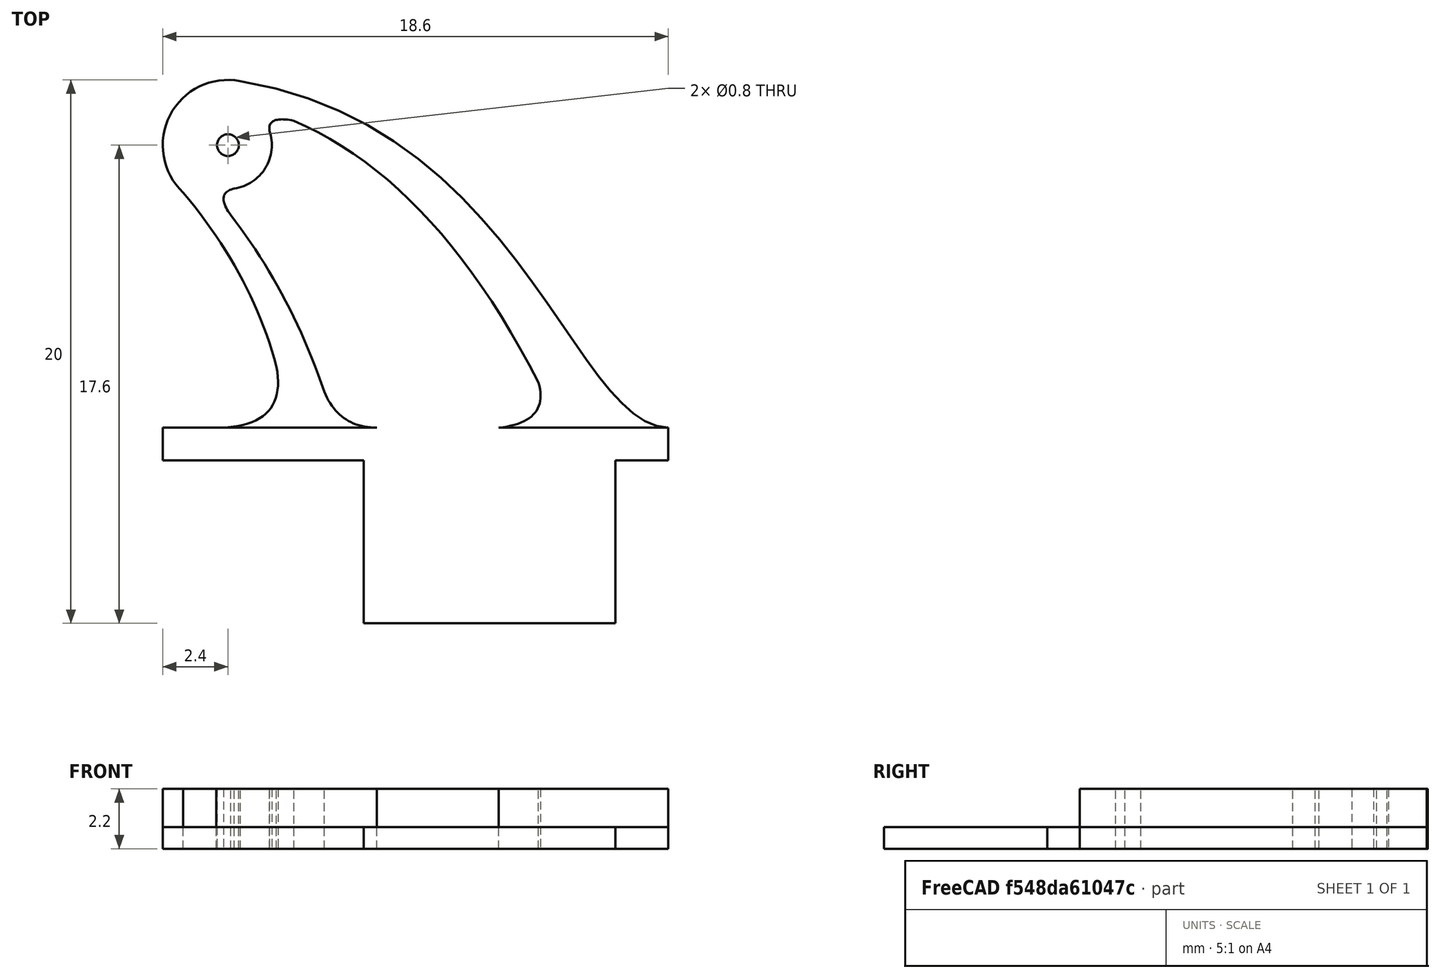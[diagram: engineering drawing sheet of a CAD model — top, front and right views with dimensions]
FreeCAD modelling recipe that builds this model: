
FCSTD DOCUMENT  (FreeCAD 0.20R0.20.2)
Label: 008
License: All rights reserved
LicenseURL: http://en.wikipedia.org/wiki/All_rights_reserved
objects: Sketcher::SketchObject×2, Part::Extrusion×2
note: 4 computed .brp shape members not serialized (recipe doc carries the construction recipe); baked Part::Feature solids carry a one-line shape summary decoded from their .brp

FEATURE [Sketcher::SketchObject] Sketch  label="main"
  FullyConstrained = true
  sketch-geometry (25):
    g0: LineSegment StartX=12.0586 StartY=-6 StartZ=0 EndX=12.0586 EndY=0 EndZ=0
    g1: LineSegment StartX=2.8 StartY=-6 StartZ=0 EndX=2.8 EndY=0 EndZ=0
    g2: LineSegment StartX=2.8 StartY=-6 StartZ=0 EndX=12.0586 EndY=-6 EndZ=0
    g3: LineSegment StartX=12.0586 StartY=0 StartZ=0 EndX=14 EndY=0 EndZ=0
    g4: LineSegment StartX=2.8 StartY=0 StartZ=0 EndX=0 EndY=0 EndZ=0
    g5: LineSegment StartX=14 StartY=0 StartZ=0 EndX=14 EndY=1.2 EndZ=0
    g6: LineSegment StartX=0 StartY=0 StartZ=0 EndX=-4.6 EndY=0 EndZ=0
    g7: Circle CenterX=-2.2 CenterY=11.6 CenterZ=0 NormalX=0 NormalY=0 NormalZ=1 AngleXU=0 Radius=0.4
    g8-g11: Circle x4 (B-spline internal-alignment scaffolding for g12; pole/knot coordinates omitted)
    g12: BSplineCurve PolesCount=4 KnotsCount=2 Degree=3 IsPeriodic=0
    g13: GeomPoint X=-1.74436 Y=13.9564 Z=0
    g14: GeomPoint X=14 Y=1.2 Z=0
    g15: ArcOfCircle CenterX=-2.2 CenterY=11.6 CenterZ=0 NormalX=0 NormalY=0 NormalZ=1 AngleXU=0 Radius=2.4 StartAngle=1.37979 EndAngle=3.95565
    g16: LineSegment StartX=-2.62672 StartY=1.2 StartZ=0 EndX=-4.6 EndY=1.2 EndZ=0
    g17: LineSegment StartX=-4.6 StartY=0 StartZ=0 EndX=-4.6 EndY=1.2 EndZ=0
    g18: Circle CenterX=-2.62672 CenterY=1.2 CenterZ=0 NormalX=0 NormalY=0 NormalZ=1 AngleXU=0 Radius=1
    g19: Circle CenterX=0 CenterY=1.2 CenterZ=0 NormalX=0 NormalY=0 NormalZ=1 AngleXU=0 Radius=1
    g20: Circle CenterX=-0.413885 CenterY=3.44541 CenterZ=0 NormalX=0 NormalY=0 NormalZ=1 AngleXU=0 Radius=1
    g21: BSplineCurve PolesCount=3 KnotsCount=2 Degree=2 IsPeriodic=0
    g22: GeomPoint X=-2.62672 Y=1.2 Z=0
    g23: GeomPoint X=-0.413885 Y=3.44541 Z=0
    g24: BSplineCurve PolesCount=3 KnotsCount=2 Degree=2 IsPeriodic=0
  constraints (52):
    c: Vertical(g0)
    c: Vertical(g1)
    c: Block(g1)
    c: Block(g0)
    c: Distance(g1) = 6
    c: Coincident(g2,g1)
    c: Horizontal(g2)
    c: Coincident(g0,g2)
    c: Block(g2)
    c: Coincident(g3,g0)
    c: Horizontal(g3)
    c: Coincident(g4,g1)
    c: Horizontal(g4)
    c: Block(g3)
    c: Block(g4)
    c: Coincident(g5,g3)
    c: Vertical(g5)
    c: Distance(g5) = 1.2
    c: Coincident(g6,g4)
    c: Horizontal(g6)
    c: Distance(g6) = 4.6
    c: Block(g7)
    c: Weight(g8) = 1
    c: Equal(g8,g9)
    c: Equal(g8,g10)
    c: Equal(g8,g11)
    c: Coincident(g12,g5)
    c: InternalAlignment(g8-g11 -> g12) x4
    c: InternalAlignment(g13,g12)
    c: InternalAlignment(g14,g12)
    c: Block(g12)
    c: Coincident(g15,g7)
    c: Coincident(g15,g12)
    c: Coincident(g15,g24)
    c: Block(g15)
    c: Horizontal(g16)
    c: Coincident(g17,g6)
    c: Vertical(g17)
    c: Coincident(g17,g16)
    c: Weight(g18) = 1
    c: Equal(g18,g19)
    c: Equal(g18,g20)
    c: InternalAlignment(g18,g21)
    c: InternalAlignment(g19,g21)
    c: InternalAlignment(g20,g21)
    c: InternalAlignment(g22,g21)
    c: InternalAlignment(g23,g21)
    c: Block(g16)
    c: Coincident(g16,g21)
    c: Coincident(g21,g24)
    c: Block(g24)
    c: Block(g21)
FEATURE [Part::Extrusion] Extrude
  Base = -> Sketch
  Dir = (0,0,1)
  DirMode = 2
  FaceMakerClass = Part::FaceMakerBullseye
  LengthFwd = 0.8
  LengthRev = 0
  Solid = true
  Symmetric = false
FEATURE [Sketcher::SketchObject] Sketch001  label="main001"
  FullyConstrained = false
  sketch-geometry (45):
    g0: Circle CenterX=-2.2 CenterY=11.6 CenterZ=0 NormalX=0 NormalY=0 NormalZ=1 AngleXU=0 Radius=0.4
    g1-g4: Circle x4 (B-spline internal-alignment scaffolding for g5; pole/knot coordinates omitted)
    g5: BSplineCurve PolesCount=4 KnotsCount=2 Degree=3 IsPeriodic=0
    g6: GeomPoint X=-1.74436 Y=13.9564 Z=0
    g7: GeomPoint X=14 Y=1.2 Z=0
    g8: ArcOfCircle CenterX=-2.2 CenterY=11.6 CenterZ=0 NormalX=0 NormalY=0 NormalZ=1 AngleXU=0 Radius=2.4 StartAngle=1.37979 EndAngle=3.95565
    g9: Circle CenterX=-2.62672 CenterY=1.2 CenterZ=0 NormalX=0 NormalY=0 NormalZ=1 AngleXU=0 Radius=1
    g10: Circle CenterX=0 CenterY=1.2 CenterZ=0 NormalX=0 NormalY=0 NormalZ=1 AngleXU=0 Radius=1
    g11: Circle CenterX=-0.413885 CenterY=3.44541 CenterZ=0 NormalX=0 NormalY=0 NormalZ=1 AngleXU=0 Radius=1
    g12: BSplineCurve PolesCount=3 KnotsCount=2 Degree=2 IsPeriodic=0
    g13: GeomPoint X=-2.62672 Y=1.2 Z=0
    g14: GeomPoint X=-0.413885 Y=3.44541 Z=0
    g15: BSplineCurve PolesCount=3 KnotsCount=2 Degree=2 IsPeriodic=0
    g16: Circle CenterX=1.34801 CenterY=2.51783 CenterZ=0 NormalX=0 NormalY=0 NormalZ=1 AngleXU=0 Radius=1
    g17: Circle CenterX=1.8831 CenterY=1.2 CenterZ=0 NormalX=0 NormalY=0 NormalZ=1 AngleXU=0 Radius=1
    g18: Circle CenterX=3.28198 CenterY=1.2 CenterZ=0 NormalX=0 NormalY=0 NormalZ=1 AngleXU=0 Radius=1
    g19: BSplineCurve PolesCount=3 KnotsCount=2 Degree=2 IsPeriodic=0
    g20: GeomPoint X=1.34801 Y=2.51783 Z=0
    g21: GeomPoint X=3.28198 Y=1.2 Z=0
    g22: Circle CenterX=9.22372 CenterY=2.86164 CenterZ=0 NormalX=0 NormalY=0 NormalZ=1 AngleXU=0 Radius=1
    g23: Circle CenterX=9.64409 CenterY=1.39848 CenterZ=0 NormalX=0 NormalY=0 NormalZ=1 AngleXU=0 Radius=1
    g24: Circle CenterX=7.76214 CenterY=1.2 CenterZ=0 NormalX=0 NormalY=0 NormalZ=1 AngleXU=0 Radius=1
    g25: BSplineCurve PolesCount=3 KnotsCount=2 Degree=2 IsPeriodic=0
    g26: GeomPoint X=9.22372 Y=2.86164 Z=0
    g27: GeomPoint X=7.76214 Y=1.2 Z=0
    g28: LineSegment StartX=-2.62672 StartY=1.2 StartZ=0 EndX=3.28198 EndY=1.2 EndZ=0
    g29: LineSegment StartX=7.76214 StartY=1.2 StartZ=0 EndX=14 EndY=1.2 EndZ=0
    g30: Circle CenterX=-0.671756 CenterY=12.1251 CenterZ=0 NormalX=0 NormalY=0 NormalZ=1 AngleXU=0 Radius=1
    g31: Circle CenterX=-0.754831 CenterY=12.699 CenterZ=0 NormalX=0 NormalY=0 NormalZ=1 AngleXU=0 Radius=1
    g32: Circle CenterX=0.224587 CenterY=12.4971 CenterZ=0 NormalX=0 NormalY=0 NormalZ=1 AngleXU=0 Radius=1
    g33: BSplineCurve PolesCount=3 KnotsCount=2 Degree=2 IsPeriodic=0
    g34: GeomPoint X=-0.671756 Y=12.1251 Z=0
    g35: GeomPoint X=0.224587 Y=12.4971 Z=0
    g36: Circle CenterX=-2.10085 CenterY=9.02995 CenterZ=0 NormalX=0 NormalY=0 NormalZ=1 AngleXU=0 Radius=1
    g37: Circle CenterX=-2.68572 CenterY=9.84108 CenterZ=0 NormalX=0 NormalY=0 NormalZ=1 AngleXU=0 Radius=1
    g38: Circle CenterX=-1.96262 CenterY=10.0016 CenterZ=0 NormalX=0 NormalY=0 NormalZ=1 AngleXU=0 Radius=1
    g39: BSplineCurve PolesCount=3 KnotsCount=2 Degree=2 IsPeriodic=0
    g40: GeomPoint X=-2.10085 Y=9.02995 Z=0
    g41: GeomPoint X=-1.96262 Y=10.0016 Z=0
    g42: ArcOfCircle CenterX=-2.2 CenterY=11.6 CenterZ=0 NormalX=0 NormalY=0 NormalZ=1 AngleXU=0 Radius=1.61593 StartAngle=4.85982 EndAngle=6.61413
    g43: BSplineCurve PolesCount=3 KnotsCount=2 Degree=2 IsPeriodic=0
    g44: BSplineCurve PolesCount=3 KnotsCount=2 Degree=2 IsPeriodic=0
  constraints (76):
    c: Block(g0)
    c: Weight(g1) = 1
    c: Equal(g1,g2)
    c: Equal(g1,g3)
    c: Equal(g1,g4)
    c: InternalAlignment(g1-g4 -> g5) x4
    c: InternalAlignment(g6,g5)
    c: InternalAlignment(g7,g5)
    c: Block(g5)
    c: Coincident(g8,g0)
    c: Coincident(g8,g5)
    c: Coincident(g8,g15)
    c: Block(g8)
    c: Weight(g9) = 1
    c: Equal(g9,g11)
    c: InternalAlignment(g9,g12)
    c: InternalAlignment(g10,g12)
    c: InternalAlignment(g11,g12)
    c: InternalAlignment(g13,g12)
    c: InternalAlignment(g14,g12)
    c: Coincident(g12,g15)
    c: Block(g15)
    c: Block(g12)
    c: Weight(g16) = 1
    c: Equal(g16,g17)
    c: Equal(g16,g18)
    c: InternalAlignment(g16,g19)
    c: InternalAlignment(g17,g19)
    c: InternalAlignment(g18,g19)
    c: InternalAlignment(g20,g19)
    c: InternalAlignment(g21,g19)
    c: Block(g19)
    c: Weight(g22) = 1
    c: Coincident(g25,g43)
    c: Equal(g22,g23)
    c: Equal(g22,g24)
    c: InternalAlignment(g22,g25)
    c: InternalAlignment(g23,g25)
    c: InternalAlignment(g24,g25)
    c: InternalAlignment(g26,g25)
    c: InternalAlignment(g27,g25)
    c: Block(g25)
    c: Coincident(g28,g19)
    c: Horizontal(g28)
    c: Coincident(g29,g25)
    c: Horizontal(g29)
    c: Weight(g30) = 1
    c: Equal(g30,g31)
    c: Equal(g30,g32)
    c: InternalAlignment(g30,g33)
    c: InternalAlignment(g31,g33)
    c: InternalAlignment(g32,g33)
    c: InternalAlignment(g34,g33)
    c: InternalAlignment(g35,g33)
    c: Weight(g36) = 1
    c: Equal(g36,g37)
    c: Equal(g36,g38)
    c: InternalAlignment(g36,g39)
    c: InternalAlignment(g37,g39)
    c: InternalAlignment(g38,g39)
    c: InternalAlignment(g40,g39)
    c: InternalAlignment(g41,g39)
    c: Coincident(g42,g0)
    c: Coincident(g42,g39)
    c: Coincident(g42,g33)
    c: Block(g42)
    c: PointOnObject(g43,g31)
    c: PointOnObject(g44,g37)
    c: Coincident(g33,g43)
    c: Coincident(g39,g44)
    c: Block(g43)
    c: Block(g44)
    c: Block(g39)
    c: Block(g33)
    c: Block(g29)
    c: Block(g28)
FEATURE [Part::Extrusion] Extrude001
  Base = -> Sketch001
  Dir = (0,0,1)
  DirMode = 2
  FaceMakerClass = Part::FaceMakerBullseye
  LengthFwd = 2.2
  LengthRev = 0
  Solid = true
  Symmetric = false
